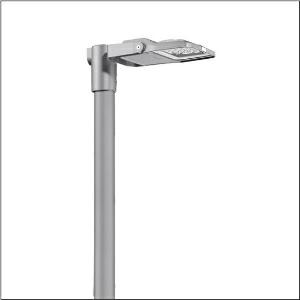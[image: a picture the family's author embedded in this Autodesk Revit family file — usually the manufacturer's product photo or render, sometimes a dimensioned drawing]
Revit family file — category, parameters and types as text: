
# Revit family: floodlight_fl_21_iq_micro___pl52_5xa7761a4d3a_5d98
name_source: partatom
category: Lighting Fixtures
units: mm (PartAtom-declared; Revit-internal decimal feet)

## family parameters
Cut with Voids When Loaded = No
Host = Face
Light Source = No
Part Type = Normal
Room Calculation Point = No
Round Connector Dimension = Use Diameter
Shared = No

## types (1)
- --- (1 x LED, 3010 lm, 23.1 W, 4000K)
    Apparent Load = 23 VA
    CIE Flux Codes = 26 60 98 100 100
    Color Rendering = 70
    Color Temperature = 4000K
    Default Elevation = 1800 mm
    Description = Floodlight FL 21 iQ micro, floodlight, primary light control with lens, of PMMA, primary optical cover: protective disc, of toughened safety glass, transparent, light distribution: PL52, light emission: direct distribution, installation type: surface-mounted, lamps: LED, High Power LED, rated values: 3.010lm | 23,1W | 130,3lm/W (begin service life); end service life: 3.010lm | 23,8W; at 50% lumin. flux: 1.505lm | 11W | 136,8lm/W, colour temperature: 4000K, colour rendering: CRI > 70, light colour: 740, light setting 1 begin service life: 100% | 3.010lm | 23,1W | 130,3lm/W | 4.000K, light setting 1 end service life: 23,8W, further light settings possible, control: optimised constant luminous flux control (CLO 2.0), Desk-Remote (wireless, voltage-free reading and setting of iQ features in the workshop via application-optimized NFC function/RFID function), Light-Fading, Smart-Wire, Night-Set, Lumen-Switch, Temp-Guard, Auto-Match, pre-setting: linear dimming characteristic, with terminal, 6-pole, mains connection: 220..240V, AC, 50/60Hz, luminaire housing, of diecast aluminium, powder-coated, SITECO metallic grey (DB 702S), corrosivity category C5 mid according to DIN EN ISO 12944suitable for swimming poolschlorine-resistant, sealing non-destructively replaceable, please order mast flange separately, mast bracket, of steel, galvanised, powder-coated, SITECO metallic grey (DB 702S), protection rating (complete): IP66, insulation class (complete): insulation class II (safety insulation), certification: CE, ENEC, VDE, protection symbol: D, impact resistance: IK07, permissible operating ambient temperature: -40..+40°C, permissible operating ambient temperature for outdoor applications: -40..+50°C, standard: DIN EN 12944, LABS conformity tested according to VDMA 24364:2018-05, packaging unit: 1 piece

Light Distribution: PL52
    Height = 65 mm
    Lamp = 1 x LED
    Lamp Light Flux = 3010 lm
    Lamp Power = 23.1 W
    Lamp count = 1
    Length = 312 mm
    Luminous efficacy = 130 lm/W
    Manufacturer = Siteco
    ModVariant = No
    Model = 5XA7761A4D3A
    Mounting Place = Pole
    Mounting Type = Pole annexe
    Number of Poles = 1
    OnlyDefault = Yes
    Power Factor = 1
    Product Name = Floodlight FL 21 iQ micro | PL52
    Product group = floodlight | pylon annexe
    ProductGroupID = 6201
    Protection Class = Protection class II
    Protection Degree = IP 66
    RLX_Detail_Level = 1
    RLX_Emergency_Light_Flux = 0 lm
    RLX_Emergency_Type = 0
    RLX_Emergency_Type_DB = No
    RlxData = <blob elided: 102265 chars, md5=f5d80921>
    Socket = socket
    Standby Power = 0 W
    System Light Flux = 3010 lm
    System Power = 23 W
    Type Comments = factory setting: luminous flux: 100 % | dim-lin: 254 | 455 mA
    Type Image = l_1007121.jpg
    URL = http://relux.com
    VarID = @adj_179027
    Voltage = 0 V
    Weight = 0.00 kg
    Width = 230 mm

## geometry (parser evidence)
native form markers: Blend x4, Sweep x11
no freeform markers — native parametric forms only
